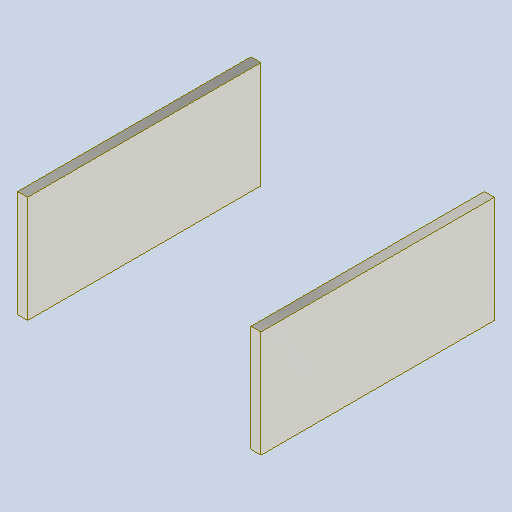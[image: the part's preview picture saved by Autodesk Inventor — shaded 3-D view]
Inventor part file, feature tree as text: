
AUTODESK INVENTOR PART (.ipt)
format: ipt  version: 2025.1 (Build 291241000, 241)  size: 217,088 bytes
history: native  units: mm
features: extrude x1, sketch x1
ambient origin geometry x8: Origin, YZ Plane, XZ Plane, XY Plane, X Axis, Y Axis, Z Axis, Center Point
bodies: Solid1 (feature_tree)
feature tree (2):
  extrude  "Extrusion1"  Depth=3.0mm
  sketch  "Sketch1"  dims[d0=73.0mm d1=3.0mm d2=32.0mm d3=16.0mm d5=0.0mm]
